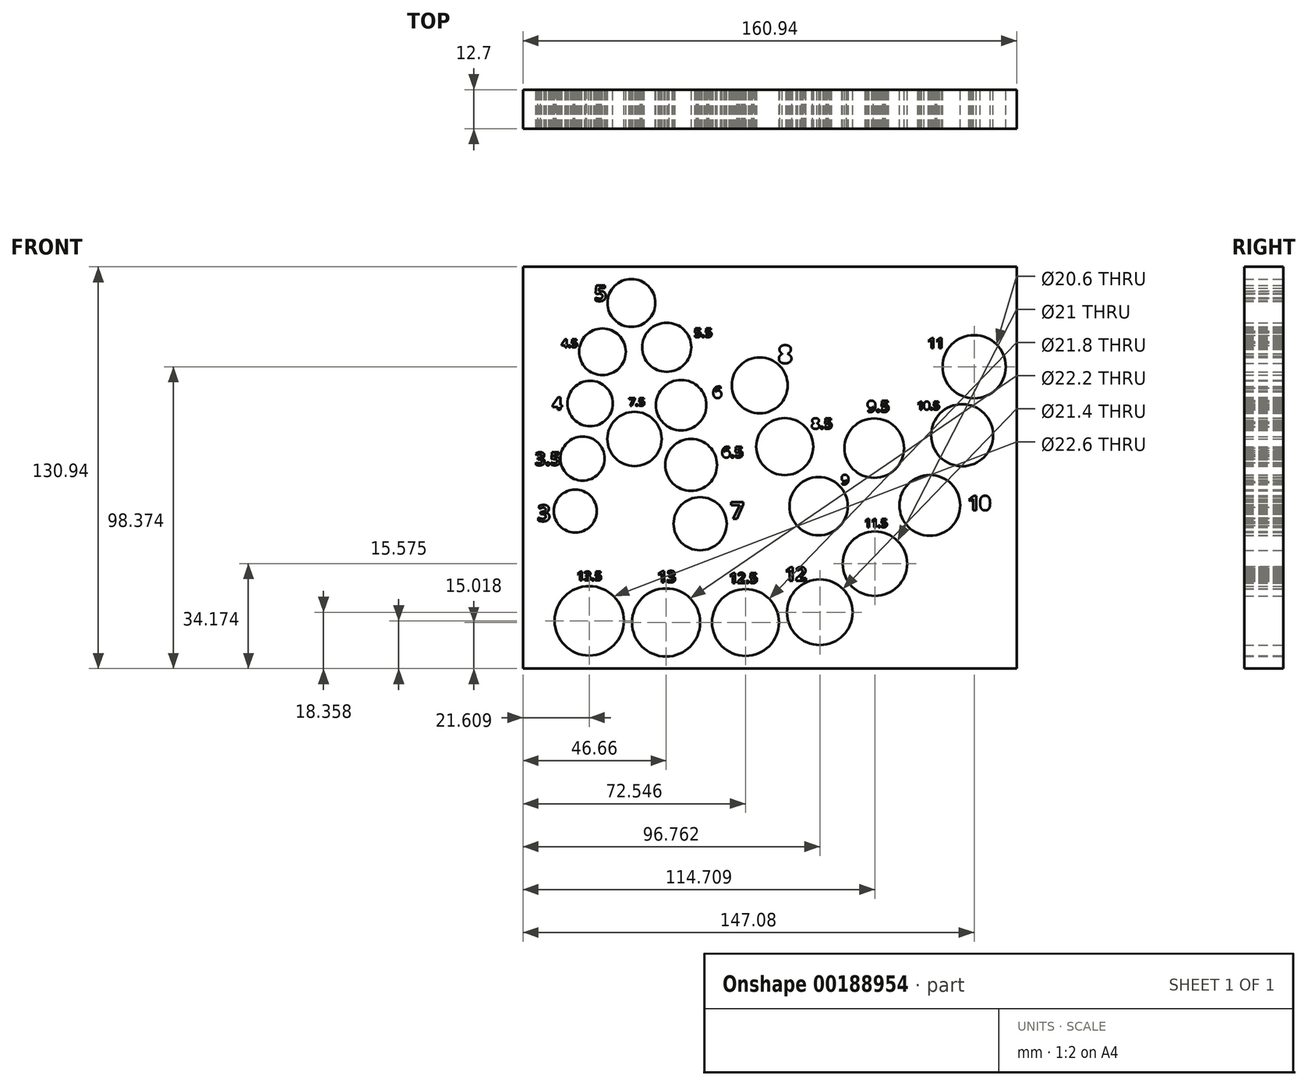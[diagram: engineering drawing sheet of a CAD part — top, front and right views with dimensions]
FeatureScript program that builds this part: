
annotation { "Feature Type Name" : "Feature", "Feature Type Description" : "" }
export const myFeature = defineFeature(function(context is Context, id is Id, definition is map)
    precondition{}
    {
        {
            var Q0;
            Q0=qCreatedBy(makeId("Front.planeOp"),FACE);
            var sketch = newSketch(context, id + "F0", { "sketchPlane" : qUnion([Q0])});
            skCircle(sketch, "E0", {"center": v(-64, -26.8) * mm, "radius": 7 * mm});
            skCircle(sketch, "E1", {"center": v(-61.64, -9.7) * mm, "radius": 7.2 * mm});
            skCircle(sketch, "E2", {"center": v(-59.15, 8.25) * mm, "radius": 7.4 * mm});
            skCircle(sketch, "E3", {"center": v(-55.15, 25.1) * mm, "radius": 7.6 * mm});
            skCircle(sketch, "E4", {"center": v(-45.72, 41.02) * mm, "radius": 7.8 * mm});
            skCircle(sketch, "E5", {"center": v(-34.21, 26.57) * mm, "radius": 8 * mm});
            skCircle(sketch, "E6", {"center": v(-29.5, 7.7) * mm, "radius": 8.22 * mm});
            skCircle(sketch, "E7", {"center": v(-26.25, -11.77) * mm, "radius": 8.45 * mm});
            skCircle(sketch, "E8", {"center": v(-23.3, -30.94) * mm, "radius": 8.65 * mm});
            skCircle(sketch, "E9", {"center": v(-44.7, -3.3) * mm, "radius": 8.85 * mm});
            skCircle(sketch, "E10", {"center": v(-3.89, 14.17) * mm, "radius": 9.1 * mm});
            skCircle(sketch, "E11", {"center": v(4.26, -5.8) * mm, "radius": 9.3 * mm});
            skCircle(sketch, "E12", {"center": v(15.32, -25.22) * mm, "radius": 9.5 * mm});
            skCircle(sketch, "E13", {"center": v(33.43, -6.3) * mm, "radius": 9.7 * mm});
            skCircle(sketch, "E14", {"center": v(51.56, -24.95) * mm, "radius": 9.9 * mm});
            skCircle(sketch, "E15", {"center": v(62.07, -2.1) * mm, "radius": 10.1 * mm});
            skCircle(sketch, "E16", {"center": v(66, 20.23) * mm, "radius": 10.3 * mm});
            skCircle(sketch, "E17", {"center": v(33.64, -43.97) * mm, "radius": 10.5 * mm});
            skCircle(sketch, "E18", {"center": v(-8.52, -63.12) * mm, "radius": 10.9 * mm});
            skCircle(sketch, "E19", {"center": v(-34.41, -63.12) * mm, "radius": 11.1 * mm});
            skText(sketch, "E20", { "text": "3", "fontName": "OpenSans-Bold.ttf"});
            skText(sketch, "E21", { "text": "3.5", "fontName": "OpenSans-Bold.ttf"});
            skText(sketch, "E22", { "text": "4", "fontName": "OpenSans-Bold.ttf"});
            skText(sketch, "E23", { "text": "5", "fontName": "OpenSans-Bold.ttf"});
            skText(sketch, "E24", { "text": "5.5", "fontName": "OpenSans-Bold.ttf"});
            skText(sketch, "E25", { "text": "6", "fontName": "OpenSans-Bold.ttf"});
            skText(sketch, "E26", { "text": "6.5", "fontName": "OpenSans-Bold.ttf"});
            skText(sketch, "E27", { "text": "7", "fontName": "OpenSans-Bold.ttf"});
            skText(sketch, "E28", { "text": "7.5", "fontName": "OpenSans-Bold.ttf"});
            skText(sketch, "E29", { "text": "8", "fontName": "OpenSans-Bold.ttf"});
            skText(sketch, "E30", { "text": "8.5", "fontName": "OpenSans-Bold.ttf"});
            skText(sketch, "E31", { "text": "9", "fontName": "OpenSans-Bold.ttf"});
            skText(sketch, "E32", { "text": "9.5", "fontName": "OpenSans-Bold.ttf"});
            skText(sketch, "E33", { "text": "10", "fontName": "OpenSans-Bold.ttf"});
            skText(sketch, "E34", { "text": "10.5", "fontName": "OpenSans-Bold.ttf"});
            skText(sketch, "E35", { "text": "11", "fontName": "OpenSans-Bold.ttf"});
            skText(sketch, "E36", { "text": "11.5", "fontName": "OpenSans-Bold.ttf"});
            skCircle(sketch, "E37", {"center": v(15.7, -59.78) * mm, "radius": 10.7 * mm});
            skCircle(sketch, "E38", {"center": v(-59.46, -62.57) * mm, "radius": 11.3 * mm});
            skText(sketch, "E39", { "text": "12", "fontName": "OpenSans-Bold.ttf"});
            skText(sketch, "E40", { "text": "12.5", "fontName": "OpenSans-Bold.ttf"});
            skText(sketch, "E41", { "text": "13", "fontName": "OpenSans-Bold.ttf"});
            skText(sketch, "E42", { "text": "13.5", "fontName": "OpenSans-Bold.ttf"});
            skLineSegment(sketch, "E43.bottom", {"start": v(-81.07, 52.8) * mm, "end": v(79.87, 52.8) * mm});
            skLineSegment(sketch, "E43.top", {"start": v(-81.07, -78.14) * mm, "end": v(79.87, -78.14) * mm});
            skLineSegment(sketch, "E43.left", {"start": v(-81.07, 52.8) * mm, "end": v(-81.07, -78.14) * mm});
            skLineSegment(sketch, "E43.right", {"start": v(79.87, 52.8) * mm, "end": v(79.87, -78.14) * mm});
            skText(sketch, "E44", { "text": "4.5", "fontName": "OpenSans-Bold.ttf"});
            const initialGuessF0  = {"E20": [-0.07635, -0.03012, 1, 0, 0.00529], "E21": [-0.07711, -0.01186, 1, 0, 0.00421], "E22": [-0.07153, 0.00626, 1, 0, 0.00409], "E23": [-0.05781, 0.04163, 1, 0, 0.00513], "E24": [-0.02522, 0.02988, 1, 0, 0.00293], "E25": [-0.0192, 0.01003, 1, 0, 0.00375], "E26": [-0.01628, -0.00936, 1, 0, 0.00354], "E27": [-0.0134, -0.0294, 1, 0, 0.00557], "E28": [-0.04654, 0.00747, 1, 0, 0.00263], "E29": [0.00209, 0.0214, 1, 0, 0.00585], "E30": [0.01293, 0, 1, 0, 0.00346], "E31": [0.02267, -0.01814, 1, 0, 0.00316], "E32": [0.03109, 0.0055, 1, 0, 0.00368], "E33": [0.06393, -0.02655, 1, 0, 0.00473], "E34": [0.0474, 0.00624, 1, 0, 0.00265], "E35": [0.05081, 0.02623, 1, 0, 0.00334], "E36": [0.03022, -0.03208, 1, 0, 0.00271], "E39": [0.00428, -0.04948, 1, 0, 0.00445], "E40": [-0.01385, -0.05026, 1, 0, 0.00334], "E41": [-0.0372, -0.05005, 1, 0, 0.00375], "E42": [-0.06348, -0.04943, 1, 0, 0.00292], "E44": [-0.06846, 0.02658, 1, 0, 0.00264]};
            skSetInitialGuess(sketch, initialGuessF0);
            skSolve(sketch);
        }
        {
            var Q0;
            Q0 = qSketchRegion(id + "F0", true);
            extrude(context, id + "F1", {"entities" : qUnion([Q0]), "depth" : 12.7 * mm});
        }
    });
